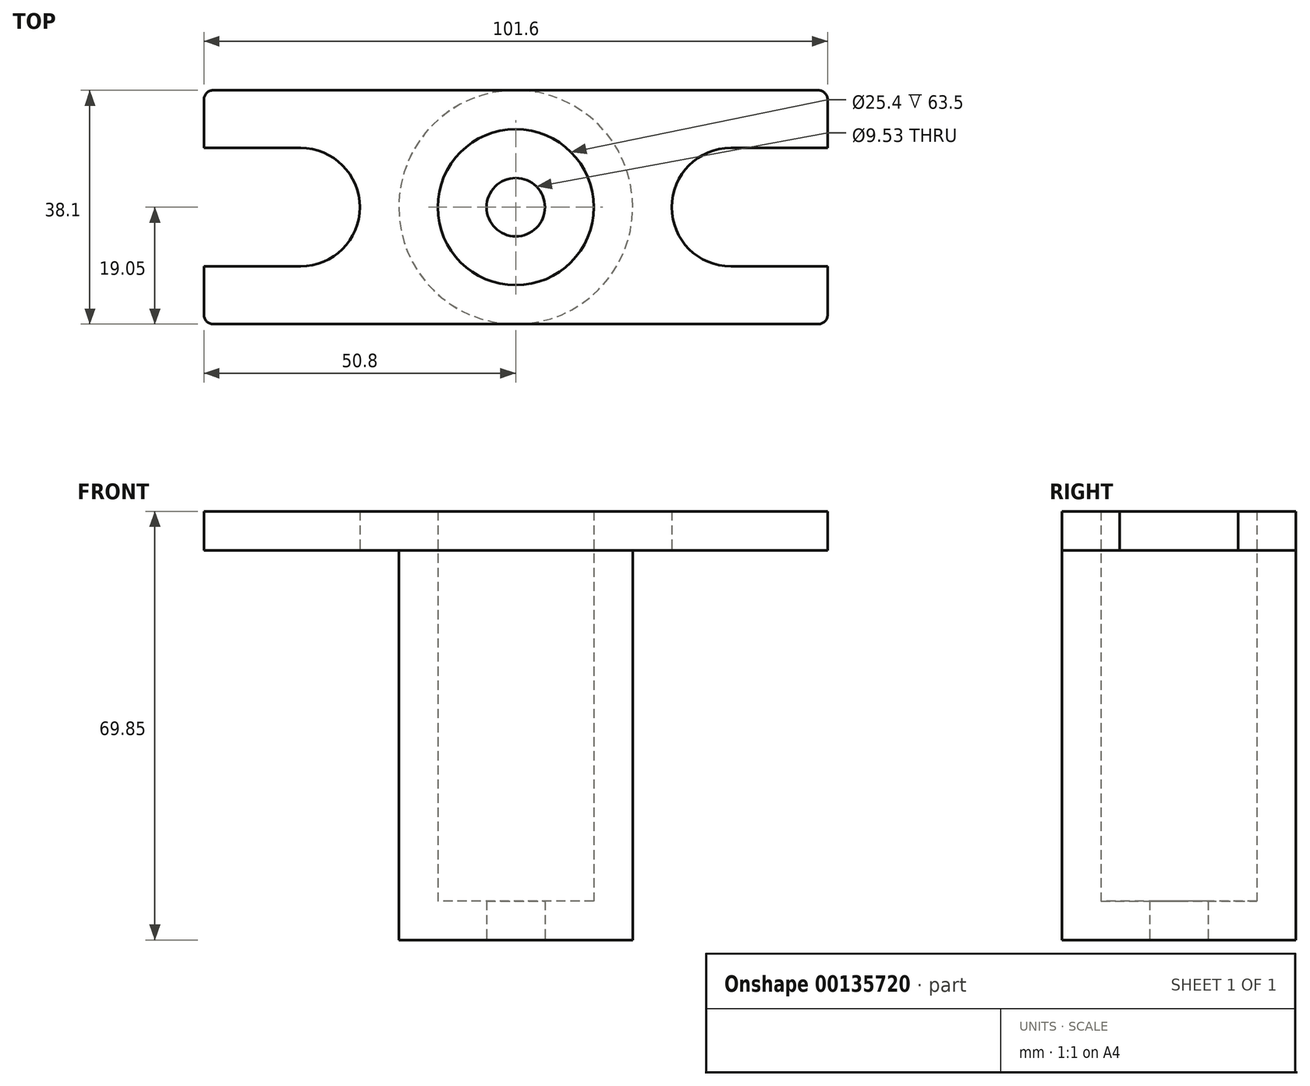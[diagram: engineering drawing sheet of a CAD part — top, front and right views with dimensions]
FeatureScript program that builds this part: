
annotation { "Feature Type Name" : "Feature", "Feature Type Description" : "" }
export const myFeature = defineFeature(function(context is Context, id is Id, definition is map)
    precondition{}
    {
        {
            var Q0;
            Q0=qCreatedBy(makeId("Top.planeOp"),FACE);
            var sketch = newSketch(context, id + "F0", { "sketchPlane" : qUnion([Q0])});
            skCircle(sketch, "E0", {"center": v(0, 0) * mm, "radius": 12.7 * mm});
            skLineSegment(sketch, "E1", {"start": v(-59.04, 0) * mm, "end": v(79.72, 0) * mm, "construction": true});
            skLineSegment(sketch, "E2", {"start": v(-50.8, 19.05) * mm, "end": v(50.8, 19.05) * mm});
            skLineSegment(sketch, "E3", {"start": v(-50.8, -19.05) * mm, "end": v(50.8, -19.05) * mm});
            skLineSegment(sketch, "E4", {"start": v(-50.8, 19.05) * mm, "end": v(-50.8, 9.65) * mm});
            skLineSegment(sketch, "E5", {"start": v(-50.8, 9.65) * mm, "end": v(-35.05, 9.65) * mm});
            skLineSegment(sketch, "E6", {"start": v(-50.8, -19.05) * mm, "end": v(-50.8, -9.65) * mm});
            skLineSegment(sketch, "E7", {"start": v(-50.8, -9.65) * mm, "end": v(-35.05, -9.65) * mm});
            skLineSegment(sketch, "E8", {"start": v(50.8, 19.05) * mm, "end": v(50.8, 9.65) * mm});
            skLineSegment(sketch, "E9", {"start": v(50.8, 9.65) * mm, "end": v(35.05, 9.65) * mm});
            skLineSegment(sketch, "E10", {"start": v(50.8, -19.05) * mm, "end": v(50.8, -9.65) * mm});
            skLineSegment(sketch, "E11", {"start": v(50.8, -9.65) * mm, "end": v(35.05, -9.65) * mm});
            skArc(sketch, "E12", {"start": v(-35.05, 9.65) * mm, "mid": v(-25.4, 0) * mm, "end": v(-35.05, -9.65) * mm});
            skLineSegment(sketch, "E13", {"start": v(0, 46.77) * mm, "end": v(0, -43.11) * mm, "construction": true});
            skArc(sketch, "E14", {"start": v(35.05, 9.65) * mm, "mid": v(25.4, 0) * mm, "end": v(35.05, -9.65) * mm});
            skSolve(sketch);
        }
        {
            var Q0;
            Q0=makeQuery(id+"F0.imprint","IMPRINT",FACE,{"disambiguationData":[TD([[makeQuery(id+"F0.imprint","IMPRINT",EDGE,{"derivedFrom":sQuery(id+"F0.wireOp",EDGE,"E0")}),-1.0]])]});
            extrude(context, id + "F1", {"entities" : qUnion([Q0]), "depth" : 6.35 * mm});
        }
        {
            var Q0;
            Q0=makeQuery(id+"F1.opExtrude","SWEPT_EDGE",EDGE,{"disambiguationData":[OSD([sQuery(id+"F0.wireOp",EDGE,"E3"),sQuery(id+"F0.wireOp",EDGE,"E6")])]});
            var Q1;
            Q1=makeQuery(id+"F1.opExtrude","SWEPT_EDGE",EDGE,{"disambiguationData":[OSD([sQuery(id+"F0.wireOp",EDGE,"E3"),sQuery(id+"F0.wireOp",EDGE,"E10")])]});
            var Q2;
            Q2=makeQuery(id+"F1.opExtrude","SWEPT_EDGE",EDGE,{"disambiguationData":[OSD([sQuery(id+"F0.wireOp",EDGE,"E2"),sQuery(id+"F0.wireOp",EDGE,"E8")])]});
            var Q3;
            Q3=makeQuery(id+"F1.opExtrude","SWEPT_EDGE",EDGE,{"disambiguationData":[OSD([sQuery(id+"F0.wireOp",EDGE,"E2"),sQuery(id+"F0.wireOp",EDGE,"E4")])]});
            fillet(context, id + "F2", {"entities" : qUnion([Q0, Q1, Q2, Q3]), "radius" : 1.52 * mm, "tangentPropagation" : true, "allowEdgeOverflow" : false});
        }
        {
            var Q0;
            Q0=makeQuery(id+"F1.opExtrude","CAP_FACE",FACE,{"disambiguationData":[OSD([sQuery(id+"F0.wireOp",EDGE,"E0"),sQuery(id+"F0.wireOp",EDGE,"E2"),sQuery(id+"F0.wireOp",EDGE,"E3"),sQuery(id+"F0.wireOp",EDGE,"E4"),sQuery(id+"F0.wireOp",EDGE,"E5"),sQuery(id+"F0.wireOp",EDGE,"E6"),sQuery(id+"F0.wireOp",EDGE,"E7"),sQuery(id+"F0.wireOp",EDGE,"E8"),sQuery(id+"F0.wireOp",EDGE,"E9"),sQuery(id+"F0.wireOp",EDGE,"E10"),sQuery(id+"F0.wireOp",EDGE,"E11"),sQuery(id+"F0.wireOp",EDGE,"E12"),sQuery(id+"F0.wireOp",EDGE,"E14")])],"isStart":true});
            var sketch = newSketch(context, id + "F3", { "sketchPlane" : qUnion([Q0])});
            skCircle(sketch, "E15", {"center": v(0, 0) * mm, "radius": 19.05 * mm});
            skCircle(sketch, "E16.0", {"center": v(0, 0) * mm, "radius": 12.7 * mm});
            skSolve(sketch);
        }
        {
            var Q0;
            Q0=makeQuery(id+"F3.imprint","IMPRINT",FACE,{"disambiguationData":[TD([[makeQuery(id+"F3.imprint","IMPRINT",EDGE,{"derivedFrom":sQuery(id+"F3.wireOp",EDGE,"E16.0")}),1.0]])]});
            extrude(context, id + "F4", {"entities" : qUnion([Q0]), "operationType" : NewBodyOperationType.ADD, "depth" : 63.5 * mm});
        }
        {
            var Q0;
            Q0=makeQuery(id+"F4.opExtrude","CAP_FACE",FACE,{"disambiguationData":[OSD([sQuery(id+"F3.wireOp",EDGE,"E15"),sQuery(id+"F3.wireOp",EDGE,"E16.0")])],"isStart":false});
            var sketch = newSketch(context, id + "F5", { "sketchPlane" : qUnion([Q0])});
            skCircle(sketch, "E17", {"center": v(0, 0) * mm, "radius": 4.76 * mm});
            skCircle(sketch, "E18.0", {"center": v(0, 0) * mm, "radius": 12.7 * mm});
            skSolve(sketch);
        }
        {
            var Q0;
            Q0=makeQuery(id+"F5.imprint","IMPRINT",FACE,{"disambiguationData":[TD([[makeQuery(id+"F5.imprint","IMPRINT",EDGE,{"derivedFrom":sQuery(id+"F5.wireOp",EDGE,"E17")}),-1.0]])]});
            extrude(context, id + "F6", {"entities" : qUnion([Q0]), "operationType" : NewBodyOperationType.ADD, "oppositeDirection" : true, "depth" : 6.35 * mm});
        }
    });
